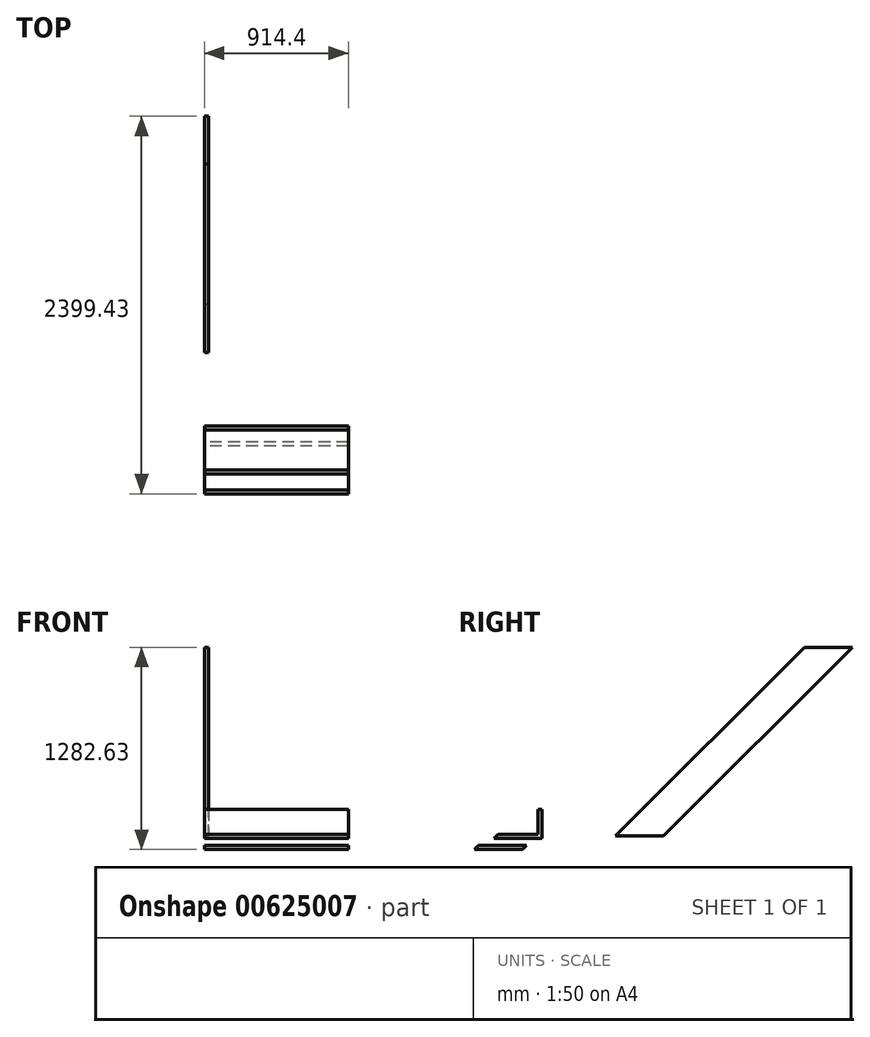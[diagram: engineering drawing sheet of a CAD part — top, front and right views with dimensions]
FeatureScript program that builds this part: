
annotation { "Feature Type Name" : "Feature", "Feature Type Description" : "" }
export const myFeature = defineFeature(function(context is Context, id is Id, definition is map)
    precondition{}
    {
        {
            var Q0;
            Q0=qCreatedBy(makeId("Right.planeOp"),FACE);
            var sketch = newSketch(context, id + "F0", { "sketchPlane" : qUnion([Q0])});
            skLineSegment(sketch, "E0", {"start": v(304.8, 0) * mm, "end": v(1502.72, 1197.92) * mm});
            skLineSegment(sketch, "E1", {"start": v(1502.72, 1197.92) * mm, "end": v(1197.92, 1197.92) * mm});
            skLineSegment(sketch, "E2", {"start": v(1197.92, 1197.92) * mm, "end": v(0, 0) * mm});
            skLineSegment(sketch, "E3", {"start": v(0, 0) * mm, "end": v(304.8, 0) * mm});
            skSolve(sketch);
        }
        {
            var Q0;
            Q0 = qSketchRegion(id + "F0", true);
            extrude(context, id + "F1", {"entities" : qUnion([Q0]), "depth" : 25.4 * mm, "offsetDistance" : 25.4 * mm});
        }
        {
            var Q0;
            Q0=qCreatedBy(makeId("Right.planeOp"),FACE);
            var sketch = newSketch(context, id + "F2", { "sketchPlane" : qUnion([Q0])});
            skLineSegment(sketch, "E4", {"start": v(-896.7, -84.7) * mm, "end": v(-591.9, -84.7) * mm});
            skLineSegment(sketch, "E5", {"start": v(-591.9, -84.7) * mm, "end": v(-566.5, -59.3) * mm});
            skLineSegment(sketch, "E6", {"start": v(-566.5, -59.3) * mm, "end": v(-871.3, -59.3) * mm});
            skLineSegment(sketch, "E7", {"start": v(-871.3, -59.3) * mm, "end": v(-896.7, -84.7) * mm});
            skSolve(sketch);
        }
        {
            var Q0;
            Q0 = qSketchRegion(id + "F2", true);
            extrude(context, id + "F3", {"entities" : qUnion([Q0]), "depth" : 914.4 * mm, "offsetDistance" : 25.4 * mm});
        }
        {
            var Q0;
            Q0=qCreatedBy(makeId("Right.planeOp"),FACE);
            var sketch = newSketch(context, id + "F4", { "sketchPlane" : qUnion([Q0])});
            skLineSegment(sketch, "E8", {"start": v(-770.94, -16.08) * mm, "end": v(-745.54, 9.32) * mm});
            skLineSegment(sketch, "E9", {"start": v(-745.54, 9.32) * mm, "end": v(-491.54, 9.32) * mm});
            skLineSegment(sketch, "E10", {"start": v(-491.54, 9.32) * mm, "end": v(-491.54, 170.3) * mm});
            skLineSegment(sketch, "E11", {"start": v(-491.54, 170.3) * mm, "end": v(-466.14, 170.3) * mm});
            skLineSegment(sketch, "E12", {"start": v(-466.14, 170.3) * mm, "end": v(-466.14, -16.08) * mm});
            skLineSegment(sketch, "E13", {"start": v(-466.14, -16.08) * mm, "end": v(-770.94, -16.08) * mm});
            skSolve(sketch);
        }
        {
            var Q0;
            Q0 = qSketchRegion(id + "F4", true);
            extrude(context, id + "F5", {"entities" : qUnion([Q0]), "depth" : 914.4 * mm, "offsetDistance" : 25.4 * mm});
        }
    });
